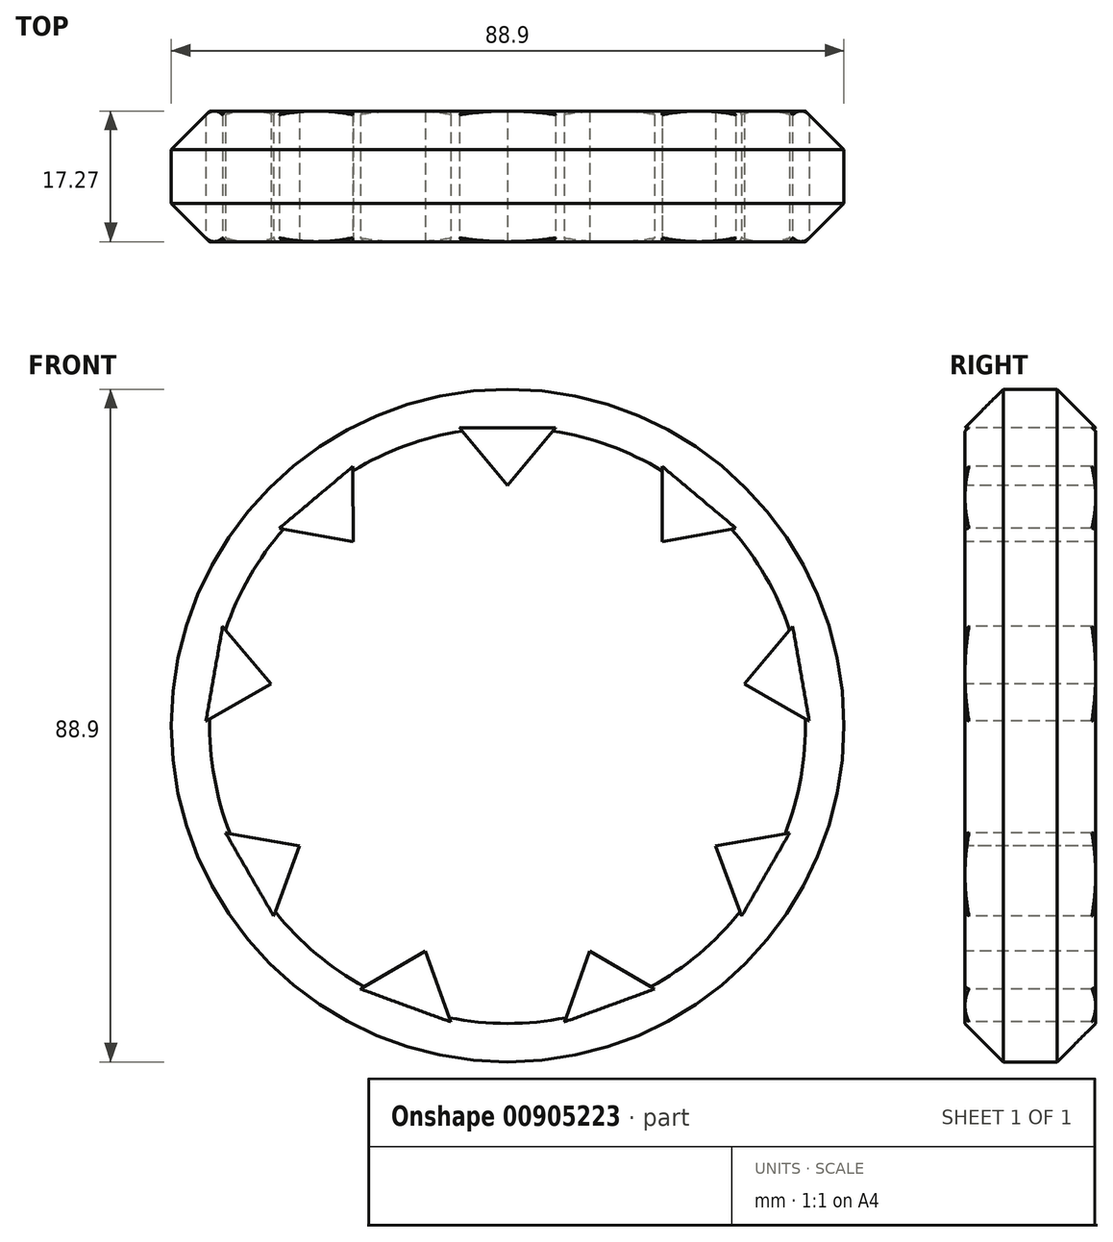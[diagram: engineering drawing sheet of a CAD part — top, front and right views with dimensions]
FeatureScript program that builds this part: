
annotation { "Feature Type Name" : "Feature", "Feature Type Description" : "" }
export const myFeature = defineFeature(function(context is Context, id is Id, definition is map)
    precondition{}
    {
        {
            var Q0;
            Q0=qCreatedBy(makeId("Front.planeOp"),FACE);
            var sketch = newSketch(context, id + "F0", { "sketchPlane" : qUnion([Q0])});
            skCircle(sketch, "E0", {"center": v(0, 0) * mm, "radius": 44.45 * mm});
            skSolve(sketch);
        }
        {
            var Q0;
            Q0=makeQuery(id+"F0.imprint","IMPRINT",FACE,{"disambiguationData":[TD([[makeQuery(id+"F0.imprint","IMPRINT",EDGE,{"derivedFrom":sQuery(id+"F0.wireOp",EDGE,"E0")}),1.0]])]});
            extrude(context, id + "F1", {"entities" : qUnion([Q0]), "depth" : 17.27 * mm, "offsetDistance" : 25.4 * mm});
        }
        {
            var Q0;
            Q0=makeQuery(id+"F1.opExtrude","CAP_FACE",FACE,{"disambiguationData":[OSD([sQuery(id+"F0.wireOp",EDGE,"E0")])],"isStart":false});
            var sketch = newSketch(context, id + "F2", { "sketchPlane" : qUnion([Q0])});
            skLineSegment(sketch, "E1", {"start": v(0, 39.37) * mm, "end": v(6.35, 39.37) * mm});
            skPoint(sketch, "E2", {"position": v(0, 31.75) * mm});
            skLineSegment(sketch, "E3", {"start": v(6.35, 39.37) * mm, "end": v(0, 31.75) * mm});
            skLineSegment(sketch, "E4.MirrorCS", {"start": v(-6.35, 39.37) * mm, "end": v(0, 31.75) * mm});
            skLineSegment(sketch, "E5.MirrorCS", {"start": v(0, 39.37) * mm, "end": v(-6.35, 39.37) * mm});
            skLineSegment(sketch, "E6.1.0", {"start": v(-20.44, 34.24) * mm, "end": v(-20.4, 24.32) * mm});
            skLineSegment(sketch, "E6.1.1", {"start": v(-30.17, 26.08) * mm, "end": v(-20.4, 24.32) * mm});
            skLineSegment(sketch, "E6.1.2", {"start": v(-25.3, 30.16) * mm, "end": v(-30.17, 26.08) * mm});
            skLineSegment(sketch, "E6.1.3", {"start": v(-25.3, 30.16) * mm, "end": v(-20.44, 34.24) * mm});
            skLineSegment(sketch, "E6.2.0", {"start": v(-37.67, 13.1) * mm, "end": v(-31.27, 5.51) * mm});
            skLineSegment(sketch, "E6.2.1", {"start": v(-39.87, 0.58) * mm, "end": v(-31.27, 5.51) * mm});
            skLineSegment(sketch, "E6.2.2", {"start": v(-38.77, 6.84) * mm, "end": v(-39.87, 0.58) * mm});
            skLineSegment(sketch, "E6.2.3", {"start": v(-38.77, 6.84) * mm, "end": v(-37.67, 13.1) * mm});
            skPoint(sketch, "E6.center", {"position": v(0, 0) * mm});
            skLineSegment(sketch, "E6.anchor1", {"start": v(0, 31.75) * mm, "end": v(0, 0) * mm, "construction": true});
            skLineSegment(sketch, "E6.anchor2", {"start": v(0, 31.75) * mm, "end": v(0, 0) * mm, "construction": true});
            skLineSegment(sketch, "E7.2.3.0", {"start": v(-37.27, -14.19) * mm, "end": v(-27.5, -15.87) * mm});
            skLineSegment(sketch, "E7.3.3.0", {"start": v(-30.92, -25.18) * mm, "end": v(-27.5, -15.87) * mm});
            skLineSegment(sketch, "E7.6.3.0", {"start": v(-34.1, -19.68) * mm, "end": v(-30.92, -25.18) * mm});
            skLineSegment(sketch, "E7.9.3.0", {"start": v(-34.1, -19.69) * mm, "end": v(-37.27, -14.19) * mm});
            skLineSegment(sketch, "E7.2.4.0", {"start": v(-19.43, -34.82) * mm, "end": v(-10.86, -29.84) * mm});
            skLineSegment(sketch, "E7.3.4.0", {"start": v(-7.5, -39.17) * mm, "end": v(-10.86, -29.84) * mm});
            skLineSegment(sketch, "E7.6.4.0", {"start": v(-13.47, -37) * mm, "end": v(-7.5, -39.17) * mm});
            skLineSegment(sketch, "E7.9.4.0", {"start": v(-13.47, -37) * mm, "end": v(-19.43, -34.82) * mm});
            skLineSegment(sketch, "E8.2.5.0", {"start": v(7.5, -39.17) * mm, "end": v(10.86, -29.84) * mm});
            skLineSegment(sketch, "E8.3.5.0", {"start": v(19.43, -34.82) * mm, "end": v(10.86, -29.84) * mm});
            skLineSegment(sketch, "E8.6.5.0", {"start": v(13.47, -37) * mm, "end": v(19.43, -34.82) * mm});
            skLineSegment(sketch, "E8.9.5.0", {"start": v(13.47, -37) * mm, "end": v(7.5, -39.17) * mm});
            skLineSegment(sketch, "E8.2.6.0", {"start": v(30.92, -25.18) * mm, "end": v(27.5, -15.87) * mm});
            skLineSegment(sketch, "E8.3.6.0", {"start": v(37.27, -14.19) * mm, "end": v(27.5, -15.88) * mm});
            skLineSegment(sketch, "E8.6.6.0", {"start": v(34.1, -19.68) * mm, "end": v(37.27, -14.19) * mm});
            skLineSegment(sketch, "E8.9.6.0", {"start": v(34.1, -19.68) * mm, "end": v(30.92, -25.18) * mm});
            skLineSegment(sketch, "E8.2.7.0", {"start": v(39.87, 0.58) * mm, "end": v(31.27, 5.51) * mm});
            skLineSegment(sketch, "E8.3.7.0", {"start": v(37.67, 13.1) * mm, "end": v(31.27, 5.51) * mm});
            skLineSegment(sketch, "E8.6.7.0", {"start": v(38.77, 6.84) * mm, "end": v(37.67, 13.1) * mm});
            skLineSegment(sketch, "E8.9.7.0", {"start": v(38.77, 6.84) * mm, "end": v(39.87, 0.58) * mm});
            skLineSegment(sketch, "E8.2.8.0", {"start": v(30.17, 26.08) * mm, "end": v(20.4, 24.32) * mm});
            skLineSegment(sketch, "E8.3.8.0", {"start": v(20.44, 34.24) * mm, "end": v(20.4, 24.32) * mm});
            skLineSegment(sketch, "E8.6.8.0", {"start": v(25.3, 30.16) * mm, "end": v(20.44, 34.24) * mm});
            skLineSegment(sketch, "E8.9.8.0", {"start": v(25.3, 30.16) * mm, "end": v(30.17, 26.08) * mm});
            skSolve(sketch);
        }
        {
            var Q0;
            Q0 = qSketchRegion(id + "F2", true);
            extrude(context, id + "F3", {"entities" : qUnion([Q0]), "operationType" : NewBodyOperationType.REMOVE, "endBound" : BoundingType.THROUGH_ALL, "oppositeDirection" : true, "depth" : 25.4 * mm, "offsetDistance" : 25.4 * mm});
        }
        {
            var Q0;
            Q0=makeQuery(id+"F1.opExtrude","CAP_EDGE",EDGE,{"disambiguationData":[OSD([sQuery(id+"F0.wireOp",EDGE,"E0")])],"isStart":false});
            var Q1;
            Q1=makeQuery(id+"F1.opExtrude","CAP_EDGE",EDGE,{"disambiguationData":[OSD([sQuery(id+"F0.wireOp",EDGE,"E0")])],"isStart":true});
            chamfer(context, id + "F4", {"entities" : qUnion([Q0, Q1]), "width" : 5.08 * mm, "tangentPropagation" : true});
        }
    });
